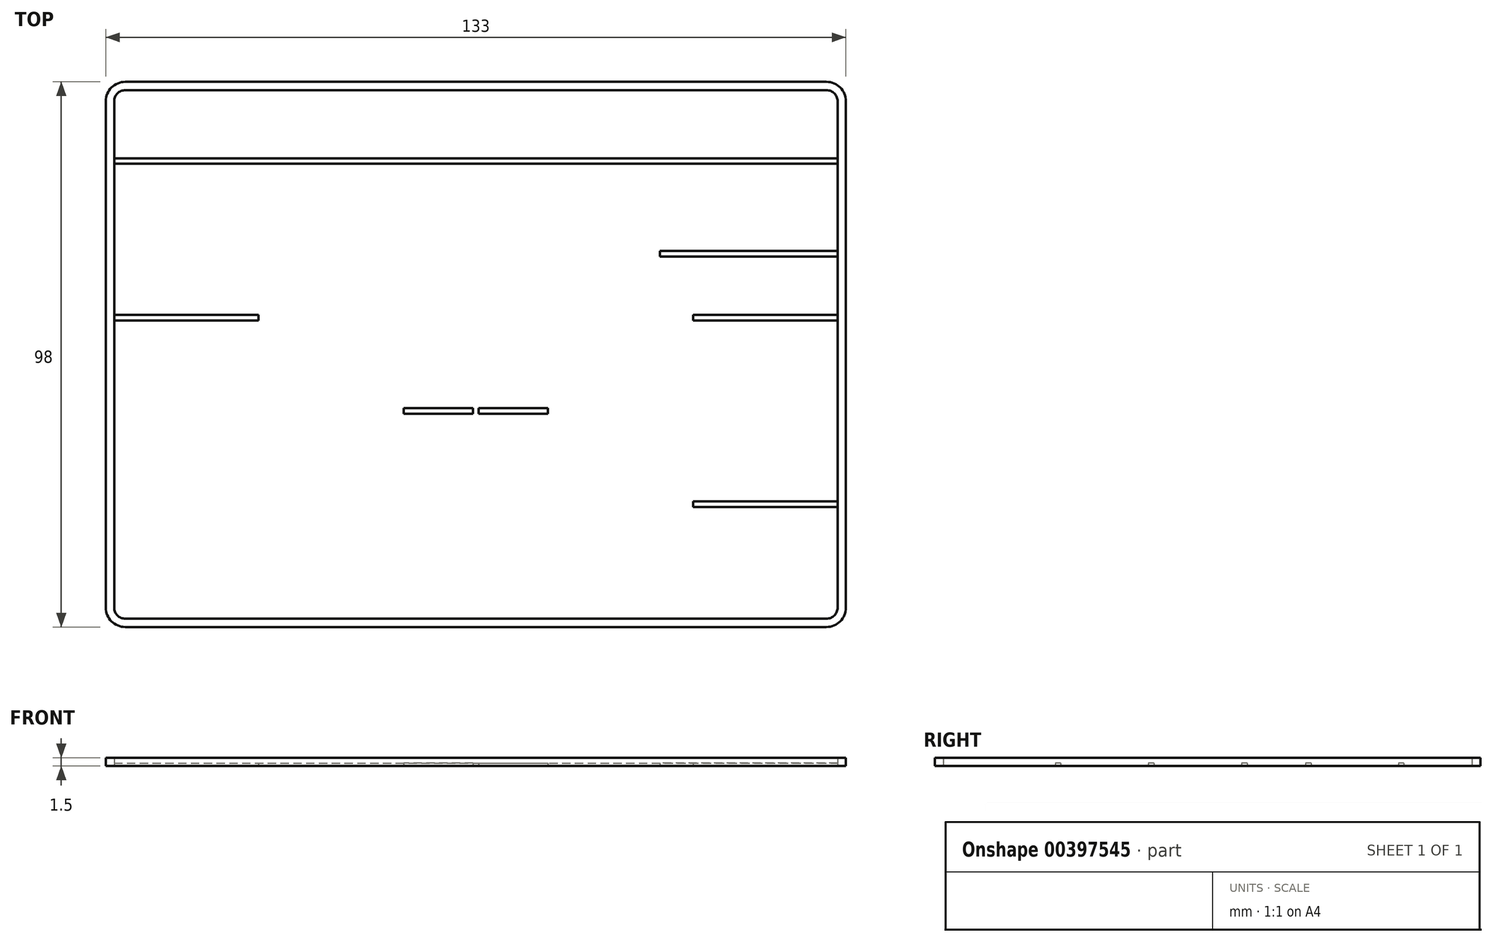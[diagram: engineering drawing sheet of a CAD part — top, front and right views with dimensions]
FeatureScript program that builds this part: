
annotation { "Feature Type Name" : "Feature", "Feature Type Description" : "" }
export const myFeature = defineFeature(function(context is Context, id is Id, definition is map)
    precondition{}
    {
        {
            var Q0;
            Q0=qCreatedBy(makeId("Top.planeOp"),FACE);
            var sketch = newSketch(context, id + "F0", { "sketchPlane" : qUnion([Q0])});
            skLineSegment(sketch, "E0.bottom", {"start": v(63, 47.5) * mm, "end": v(-63, 47.5) * mm});
            skLineSegment(sketch, "E0.top", {"start": v(63, -47.5) * mm, "end": v(-63, -47.5) * mm});
            skLineSegment(sketch, "E0.left", {"start": v(65, 45.5) * mm, "end": v(65, -45.5) * mm});
            skLineSegment(sketch, "E0.right", {"start": v(-65, 45.5) * mm, "end": v(-65, -45.5) * mm});
            skPoint(sketch, "E0.middle", {"position": v(0, 0) * mm});
            skPoint(sketch, "E1.visualSharp", {"position": v(-65, -47.5) * mm});
            skArc(sketch, "E1.filletArc", {"start": v(-65, -45.5) * mm, "mid": v(-64.41, -46.91) * mm, "end": v(-63, -47.5) * mm});
            skPoint(sketch, "E2.visualSharp", {"position": v(65, -47.5) * mm});
            skArc(sketch, "E2.filletArc", {"start": v(63, -47.5) * mm, "mid": v(64.41, -46.91) * mm, "end": v(65, -45.5) * mm});
            skPoint(sketch, "E3.visualSharp", {"position": v(65, 47.5) * mm});
            skArc(sketch, "E3.filletArc", {"start": v(65, 45.5) * mm, "mid": v(64.41, 46.91) * mm, "end": v(63, 47.5) * mm});
            skPoint(sketch, "E4.visualSharp", {"position": v(-65, 47.5) * mm});
            skArc(sketch, "E4.filletArc", {"start": v(-63, 47.5) * mm, "mid": v(-64.41, 46.91) * mm, "end": v(-65, 45.5) * mm});
            skArc(sketch, "E5.0", {"start": v(63, -49) * mm, "mid": v(65.47, -47.97) * mm, "end": v(66.5, -45.5) * mm});
            skLineSegment(sketch, "E5.1", {"start": v(66.5, 45.5) * mm, "end": v(66.5, -45.5) * mm});
            skLineSegment(sketch, "E5.2", {"start": v(63, -49) * mm, "end": v(-63, -49) * mm});
            skArc(sketch, "E5.3", {"start": v(66.5, 45.5) * mm, "mid": v(65.47, 47.97) * mm, "end": v(63, 49) * mm});
            skArc(sketch, "E5.4", {"start": v(-66.5, -45.5) * mm, "mid": v(-65.47, -47.97) * mm, "end": v(-63, -49) * mm});
            skLineSegment(sketch, "E5.5", {"start": v(-66.5, 45.5) * mm, "end": v(-66.5, -45.5) * mm});
            skArc(sketch, "E5.6", {"start": v(-63, 49) * mm, "mid": v(-65.47, 47.97) * mm, "end": v(-66.5, 45.5) * mm});
            skLineSegment(sketch, "E5.7", {"start": v(63, 49) * mm, "end": v(-63, 49) * mm});
            skLineSegment(sketch, "E6.bottom", {"start": v(-65, 35.26) * mm, "end": v(65, 35.26) * mm});
            skLineSegment(sketch, "E6.top", {"start": v(-65, 34.26) * mm, "end": v(65, 34.26) * mm});
            skLineSegment(sketch, "E6.left", {"start": v(-65, 35.26) * mm, "end": v(-65, 34.26) * mm});
            skLineSegment(sketch, "E6.right", {"start": v(65, 35.26) * mm, "end": v(65, 34.26) * mm});
            skLineSegment(sketch, "E7.bottom", {"start": v(65, 18.61) * mm, "end": v(33.1, 18.61) * mm});
            skLineSegment(sketch, "E7.top", {"start": v(65, 17.61) * mm, "end": v(33.1, 17.61) * mm});
            skLineSegment(sketch, "E7.left", {"start": v(65, 18.61) * mm, "end": v(65, 17.61) * mm});
            skLineSegment(sketch, "E7.right", {"start": v(33.1, 18.61) * mm, "end": v(33.1, 17.61) * mm});
            skLineSegment(sketch, "E8.bottom", {"start": v(-0.5, 47.5) * mm, "end": v(0.5, 47.5) * mm});
            skLineSegment(sketch, "E8.top", {"start": v(-0.5, -47.5) * mm, "end": v(0.5, -47.5) * mm});
            skLineSegment(sketch, "E8.left", {"start": v(-0.5, 47.5) * mm, "end": v(-0.5, -47.5) * mm});
            skLineSegment(sketch, "E8.right", {"start": v(0.5, 47.5) * mm, "end": v(0.5, -47.5) * mm});
            skPoint(sketch, "E9", {"position": v(0, 47.5) * mm});
            skLineSegment(sketch, "E10.MirrorCS", {"start": v(-65, 18.61) * mm, "end": v(-65, 17.61) * mm});
            skLineSegment(sketch, "E11.MirrorCS", {"start": v(-33.1, 18.61) * mm, "end": v(-33.1, 17.61) * mm});
            skLineSegment(sketch, "E12.MirrorCS", {"start": v(-65, 18.61) * mm, "end": v(-33.1, 18.61) * mm});
            skLineSegment(sketch, "E13.MirrorCS", {"start": v(-65, 17.61) * mm, "end": v(-33.1, 17.61) * mm});
            skLineSegment(sketch, "E14.bottom", {"start": v(65, 7.1) * mm, "end": v(39.06, 7.1) * mm});
            skLineSegment(sketch, "E14.top", {"start": v(65, 6.1) * mm, "end": v(39.06, 6.1) * mm});
            skLineSegment(sketch, "E14.left", {"start": v(65, 7.1) * mm, "end": v(65, 6.1) * mm});
            skLineSegment(sketch, "E14.right", {"start": v(39.06, 7.1) * mm, "end": v(39.06, 6.1) * mm});
            skLineSegment(sketch, "E15.bottom", {"start": v(65, -26.4) * mm, "end": v(39.06, -26.4) * mm});
            skLineSegment(sketch, "E15.top", {"start": v(65, -27.4) * mm, "end": v(39.06, -27.4) * mm});
            skLineSegment(sketch, "E15.left", {"start": v(65, -26.4) * mm, "end": v(65, -27.4) * mm});
            skLineSegment(sketch, "E15.right", {"start": v(39.06, -26.4) * mm, "end": v(39.06, -27.4) * mm});
            skLineSegment(sketch, "E16.bottom", {"start": v(0.5, -9.65) * mm, "end": v(12.96, -9.65) * mm});
            skLineSegment(sketch, "E16.top", {"start": v(0.5, -10.65) * mm, "end": v(12.96, -10.65) * mm});
            skLineSegment(sketch, "E16.left", {"start": v(0.5, -9.65) * mm, "end": v(0.5, -10.65) * mm});
            skLineSegment(sketch, "E16.right", {"start": v(12.96, -9.65) * mm, "end": v(12.96, -10.65) * mm});
            skPoint(sketch, "E17", {"position": v(12.96, -10.15) * mm});
            skLineSegment(sketch, "E18.MirrorCS", {"start": v(-0.5, -10.65) * mm, "end": v(-12.96, -10.65) * mm});
            skLineSegment(sketch, "E19.MirrorCS", {"start": v(-0.5, -9.65) * mm, "end": v(-12.96, -9.65) * mm});
            skLineSegment(sketch, "E20.MirrorCS", {"start": v(-12.96, -9.65) * mm, "end": v(-12.96, -10.65) * mm});
            skLineSegment(sketch, "E21.MirrorCS", {"start": v(-39.06, 7.1) * mm, "end": v(-39.06, 6.1) * mm});
            skLineSegment(sketch, "E22.MirrorCS", {"start": v(-65, -26.4) * mm, "end": v(-65, -27.4) * mm});
            skLineSegment(sketch, "E23.MirrorCS", {"start": v(-39.06, -26.4) * mm, "end": v(-39.06, -27.4) * mm});
            skLineSegment(sketch, "E24.MirrorCS", {"start": v(-65, 7.1) * mm, "end": v(-65, 6.1) * mm});
            skPoint(sketch, "E25.MirrorP", {"position": v(-12.96, -10.15) * mm});
            skLineSegment(sketch, "E26.MirrorCS", {"start": v(-65, 7.1) * mm, "end": v(-39.06, 7.1) * mm});
            skLineSegment(sketch, "E27.MirrorCS", {"start": v(-65, 6.1) * mm, "end": v(-39.06, 6.1) * mm});
            skLineSegment(sketch, "E28.MirrorCS", {"start": v(-65, -26.4) * mm, "end": v(-39.06, -26.4) * mm});
            skLineSegment(sketch, "E29.MirrorCS", {"start": v(-65, -27.4) * mm, "end": v(-39.06, -27.4) * mm});
            skLineSegment(sketch, "E30", {"start": v(-12.96, -10.15) * mm, "end": v(12.96, -10.15) * mm, "construction": true});
            skLineSegment(sketch, "E31.MirrorCS", {"start": v(65, -38.91) * mm, "end": v(65, -37.91) * mm});
            skLineSegment(sketch, "E32.MirrorCS", {"start": v(33.1, -38.91) * mm, "end": v(33.1, -37.91) * mm});
            skLineSegment(sketch, "E33.MirrorCS", {"start": v(65, -37.91) * mm, "end": v(33.1, -37.91) * mm});
            skLineSegment(sketch, "E34.MirrorCS", {"start": v(65, -38.91) * mm, "end": v(33.1, -38.91) * mm});
            skLineSegment(sketch, "E35.MirrorCS", {"start": v(-65, -38.91) * mm, "end": v(-65, -37.91) * mm});
            skLineSegment(sketch, "E36.MirrorCS", {"start": v(-33.1, -38.91) * mm, "end": v(-33.1, -37.91) * mm});
            skLineSegment(sketch, "E37.MirrorCS", {"start": v(-65, -38.91) * mm, "end": v(-33.1, -38.91) * mm});
            skLineSegment(sketch, "E38.MirrorCS", {"start": v(-65, -37.91) * mm, "end": v(-33.1, -37.91) * mm});
            skSolve(sketch);
        }
        {
            var Q0;
            Q0=makeQuery(id+"F0.imprint","IMPRINT",FACE,{"disambiguationData":[TD([[makeQuery(id+"F0.imprint","IMPRINT",EDGE,{"derivedFrom":sQuery(id+"F0.wireOp",EDGE,"E0.bottom")}),-1.0]])]});
            extrude(context, id + "F1", {"entities" : qUnion([Q0]), "depth" : 1.5 * mm});
        }
        {
            var Q0;
            Q0=makeQuery(id+"F0.imprint","IMPRINT",FACE,{"disambiguationData":[TD([[makeQuery(id+"F0.imprint","IMPRINT",EDGE,{"derivedFrom":sQuery(id+"F0.wireOp",EDGE,"E6.bottom")}),-1.0]])]});
            var Q1;
            Q1=makeQuery(id+"F0.imprint","IMPRINT",FACE,{"disambiguationData":[TD([[makeQuery(id+"F0.imprint","IMPRINT",EDGE,{"derivedFrom":sQuery(id+"F0.wireOp",EDGE,"E7.bottom")}),1.0]])]});
            var Q2;
            {var subQ5=sQuery(id+"F0.wireOp",EDGE,"E8.top");Q2=makeQuery(id+"F0.imprint","IMPRINT",FACE,{"disambiguationData":[TD([[makeQuery(id+"F0.imprint","IMPRINT",EDGE,{"derivedFrom":subQ5}),1.0]])]});}
            var Q3;
            {var subQ5=sQuery(id+"F0.wireOp",EDGE,"E8.bottom");Q3=makeQuery(id+"F0.imprint","IMPRINT",FACE,{"disambiguationData":[TD([[makeQuery(id+"F0.imprint","IMPRINT",EDGE,{"derivedFrom":subQ5}),-1.0]])]});}
            var Q4;
            Q4=makeQuery(id+"F0.imprint","IMPRINT",FACE,{"disambiguationData":[TD([[makeQuery(id+"F0.imprint","IMPRINT",EDGE,{"derivedFrom":sQuery(id+"F0.wireOp",EDGE,"E10.MirrorCS")}),1.0]])]});
            var Q5;
            Q5=makeQuery(id+"F0.imprint","IMPRINT",FACE,{"disambiguationData":[TD([[makeQuery(id+"F0.imprint","IMPRINT",EDGE,{"derivedFrom":sQuery(id+"F0.wireOp",EDGE,"E14.bottom")}),1.0]])]});
            var Q6;
            Q6=makeQuery(id+"F0.imprint","IMPRINT",FACE,{"disambiguationData":[TD([[makeQuery(id+"F0.imprint","IMPRINT",EDGE,{"derivedFrom":sQuery(id+"F0.wireOp",EDGE,"E15.bottom")}),1.0]])]});
            var Q7;
            Q7=makeQuery(id+"F0.imprint","IMPRINT",FACE,{"disambiguationData":[TD([[makeQuery(id+"F0.imprint","IMPRINT",EDGE,{"derivedFrom":sQuery(id+"F0.wireOp",EDGE,"E16.bottom")}),-1.0]])]});
            var Q8;
            Q8=makeQuery(id+"F0.imprint","IMPRINT",FACE,{"disambiguationData":[TD([[makeQuery(id+"F0.imprint","IMPRINT",EDGE,{"derivedFrom":sQuery(id+"F0.wireOp",EDGE,"E21.MirrorCS")}),-1.0]])]});
            var Q9;
            {var subQ0=sQuery(id+"F0.wireOp",EDGE,"E18.MirrorCS");Q9=makeQuery(id+"F0.imprint","IMPRINT",FACE,{"disambiguationData":[TD([[makeQuery(id+"F0.imprint","IMPRINT",EDGE,{"derivedFrom":subQ0}),-1.0]])]});}
            var Q10;
            Q10=makeQuery(id+"F0.imprint","IMPRINT",FACE,{"disambiguationData":[TD([[makeQuery(id+"F0.imprint","IMPRINT",EDGE,{"derivedFrom":sQuery(id+"F0.wireOp",EDGE,"E22.MirrorCS")}),1.0]])]});
            var Q11;
            Q11=makeQuery(id+"F0.imprint","IMPRINT",FACE,{"disambiguationData":[TD([[makeQuery(id+"F0.imprint","IMPRINT",EDGE,{"derivedFrom":sQuery(id+"F0.wireOp",EDGE,"E35.MirrorCS")}),-1.0]])]});
            var Q12;
            Q12=makeQuery(id+"F0.imprint","IMPRINT",FACE,{"disambiguationData":[TD([[makeQuery(id+"F0.imprint","IMPRINT",EDGE,{"derivedFrom":sQuery(id+"F0.wireOp",EDGE,"E31.MirrorCS")}),1.0]])]});
            extrude(context, id + "F2", {"entities" : qUnion([Q0, Q1, Q2, Q3, Q4, Q5, Q6, Q7, Q8, Q9, Q10, Q11, Q12]), "operationType" : NewBodyOperationType.ADD, "depth" : 0.5 * mm});
        }
    });
